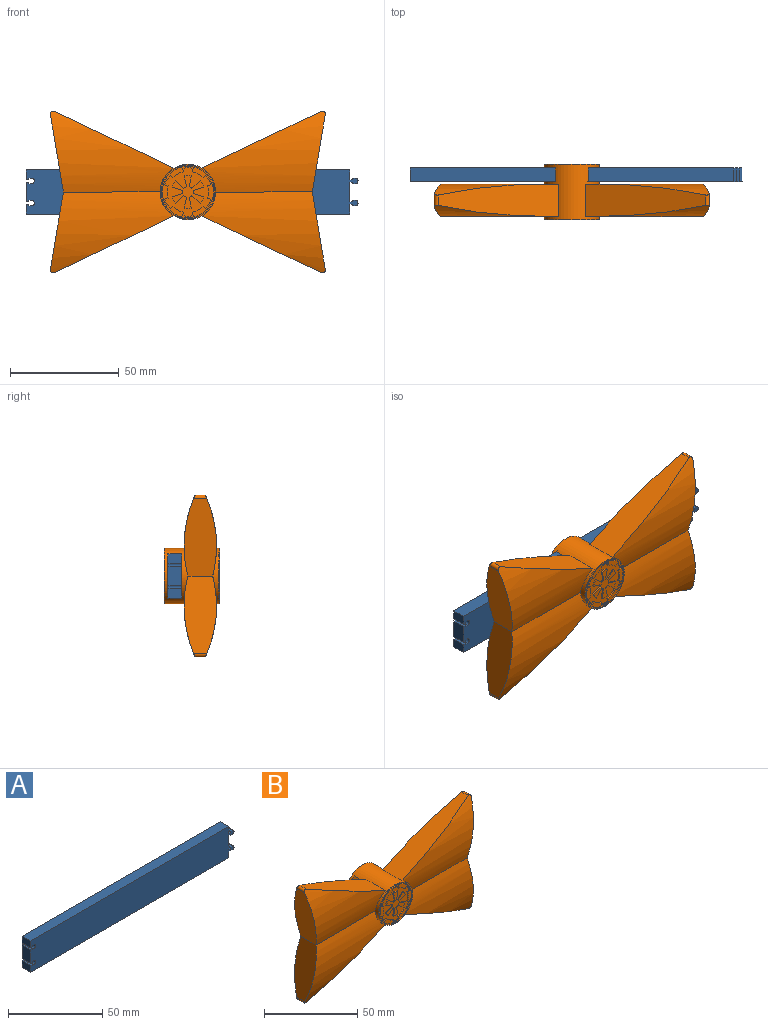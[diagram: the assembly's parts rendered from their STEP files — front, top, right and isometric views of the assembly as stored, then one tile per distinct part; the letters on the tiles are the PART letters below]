
ASSEMBLY  parts=2 mates=1
PART A: 38 faces, bbox 152.4x6.4x20.3 mm
  f0: plane 6.35x1.27mm, normal (0,0,1), area 8.1mm2, adj f1,f35,f36,f37
  f1: plane 6.35x0.64mm, normal (-1,0,0), area 4mm2, adj f0,f2,f36,f37
  f2: plane 6.35x1.27mm, normal (0,0,1), area 8.1mm2, adj f1,f3,f36,f37
  f3: plane 6.35x4.45mm, normal (1,0,0), area 28.2mm2, adj f2,f4,f36,f37
  f4: plane 148.59x6.35mm, normal (0,0,1), area 943.5mm2, adj f3,f5,f36,f37
  f5: plane 6.35x4.45mm, normal (-1,0,0), area 28.2mm2, adj f4,f6,f36,f37
  f6: plane 6.35x1.27mm, normal (0,0,-1), area 8.1mm2, adj f5,f7,f36,f37
  f7: plane 6.35x0.64mm, normal (1,0,0), area 4mm2, adj f6,f8,f36,f37
  f8: plane 6.35x1.27mm, normal (0,0,-1), area 8.1mm2, adj f7,f9,f36,f37
  f9: cylinder r=1.27mm len=6.35mm, axis (0,1,0), area 25.3mm2, adj f8,f10,f36,f37
  f10: plane 6.35x1.27mm, normal (0,0,1), area 8.1mm2, adj f9,f11,f36,f37
  f11: plane 6.35x0.64mm, normal (1,0,0), area 4mm2, adj f10,f12,f36,f37
  f12: plane 6.35x1.27mm, normal (0,0,1), area 8.1mm2, adj f11,f13,f36,f37
  f13: plane 8.89x6.35mm, normal (-1,0,0), area 56.5mm2, adj f12,f14,f36,f37
  f14: plane 6.35x1.27mm, normal (0,0,-1), area 8.1mm2, adj f13,f15,f36,f37
  f15: plane 6.35x0.64mm, normal (1,0,0), area 4mm2, adj f14,f16,f36,f37
  f16: plane 6.35x1.27mm, normal (0,0,-1), area 8.1mm2, adj f15,f17,f36,f37
  f17: cylinder r=1.27mm len=6.35mm, axis (0,1,0), area 25.3mm2, adj f16,f18,f36,f37
  f18: plane 6.35x1.27mm, normal (0,0,1), area 8.1mm2, adj f17,f19,f36,f37
  f19: plane 6.35x0.64mm, normal (1,0,0), area 4mm2, adj f18,f20,f36,f37
  f20: plane 6.35x1.27mm, normal (0,0,1), area 8.1mm2, adj f19,f21,f36,f37
  f21: plane 6.35x4.45mm, normal (-1,0,0), area 28.2mm2, adj f20,f22,f36,f37
  f22: plane 148.59x6.35mm, normal (0,0,-1), area 943.5mm2, adj f21,f23,f36,f37
  f23: plane 6.35x4.45mm, normal (1,0,0), area 28.2mm2, adj f22,f24,f36,f37
  f24: plane 6.35x1.27mm, normal (0,0,-1), area 8.1mm2, adj f23,f25,f36,f37
  f25: plane 6.35x0.64mm, normal (-1,0,0), area 4mm2, adj f24,f26,f36,f37
  f26: plane 6.35x1.27mm, normal (0,0,-1), area 8.1mm2, adj f25,f27,f36,f37
  f27: cylinder r=1.27mm len=6.35mm, axis (0,1,0), area 25.3mm2, adj f26,f28,f36,f37
  f28: plane 6.35x1.27mm, normal (0,0,1), area 8.1mm2, adj f27,f29,f36,f37
  f29: plane 6.35x0.64mm, normal (-1,0,0), area 4mm2, adj f28,f30,f36,f37
  f30: plane 6.35x1.27mm, normal (0,0,1), area 8.1mm2, adj f29,f31,f36,f37
  f31: plane 8.89x6.35mm, normal (1,0,0), area 56.5mm2, adj f30,f32,f36,f37
  f32: plane 6.35x1.27mm, normal (0,0,-1), area 8.1mm2, adj f31,f33,f36,f37
  f33: plane 6.35x0.64mm, normal (-1,0,0), area 4mm2, adj f32,f34,f36,f37
  f34: plane 6.35x1.27mm, normal (0,0,-1), area 8.1mm2, adj f33,f35,f36,f37
  f35: cylinder r=1.27mm len=6.35mm, axis (0,1,0), area 25.3mm2, adj f0,f34,f36,f37
  f36: plane 152.4x20.32mm, normal (0,-1,0), area 3019.3mm2, adj f0,f1,f2,f3,f4,f5,f6,f7
  f37: plane 152.4x20.32mm, normal (0,1,0), area 3019.3mm2, adj f0,f1,f2,f3,f4,f5,f6,f7
PART B: 108 faces, bbox 126.2x25.4x74.4 mm
  f0: cylinder r=12.7mm len=25.4mm, axis (0,1,0), area 1002.8mm2, adj f1,f2,f3,f4,f5,f8,f9,f16
  f1: plane 25.4x25.4mm, normal (0,-1,0), area 34.8mm2, adj f0,f94
  f2: cylinder r=55.88mm len=56.77mm, axis (1,0,0), area 1247.2mm2, adj f0,f3,f6,f7,f8
  f3: cylinder r=55.88mm len=56.77mm, axis (1,0,0), area 1247.2mm2, adj f0,f2,f9,f10,f11
  f4: cylinder r=55.88mm len=56.77mm, axis (1,0,0), area 1247.2mm2, adj f0,f5,f6,f7,f8
  f5: cylinder r=55.88mm len=56.77mm, axis (1,0,0), area 1247.2mm2, adj f0,f4,f9,f10,f11
  f6: plane 35.7x14.91mm, normal (-0.99,0,0.16), area 458.5mm2, adj f2,f4,f7,f11
  f7: cylinder r=1.27mm len=5.99mm, axis (0,1,0), area 14mm2, adj f2,f4,f6,f8
  f8: plane 54.95x26.06mm, normal (0.43,0,-0.9), area 726.8mm2, adj f0,f2,f4,f7
  f9: plane 54.95x26.06mm, normal (0.43,0,0.9), area 726.8mm2, adj f0,f3,f5,f10
  f10: cylinder r=1.27mm len=5.99mm, axis (0,1,0), area 14mm2, adj f3,f5,f9,f11
  f11: plane 35.7x14.91mm, normal (-0.99,0,-0.16), area 458.5mm2, adj f3,f5,f6,f10
  f12: plane 35.7x14.91mm, normal (0.99,0,0.16), area 458.5mm2, adj f13,f15,f17,f19
  f13: cylinder r=1.27mm len=5.99mm, axis (0,1,0), area 14mm2, adj f12,f17,f19,f21
  f14: cylinder r=1.27mm len=5.99mm, axis (0,1,0), area 14mm2, adj f15,f16,f18,f20
  f15: plane 35.7x14.91mm, normal (0.99,0,-0.16), area 458.5mm2, adj f12,f14,f16,f18
  f16: cylinder r=55.88mm len=56.77mm, axis (1,0,0), area 1247.2mm2, adj f0,f14,f15,f17,f20
  f17: cylinder r=55.88mm len=56.77mm, axis (1,0,0), area 1247.2mm2, adj f0,f12,f13,f16,f21
  f18: cylinder r=55.88mm len=56.77mm, axis (1,0,0), area 1247.2mm2, adj f0,f14,f15,f19,f20
  f19: cylinder r=55.88mm len=56.77mm, axis (1,0,0), area 1247.2mm2, adj f0,f12,f13,f18,f21
  f20: plane 54.95x26.06mm, normal (-0.43,0,0.9), area 726.8mm2, adj f0,f14,f16,f18
  f21: plane 54.95x26.06mm, normal (-0.43,0,-0.9), area 726.8mm2, adj f0,f13,f17,f19
  f22: plane 0.64x0.53mm, normal (0.55,0,-0.83), area 0.4mm2, adj f23,f87,f95,f101
  f23: cylinder r=11.11mm len=1.68mm, axis (0,-1,0), area 1.3mm2, adj f22,f24,f95,f101
  f24: plane 1.17x1.07mm, normal (0.68,0,-0.74), area 1mm2, adj f23,f25,f95,f101
  f25: cylinder r=9.53mm len=4.96mm, axis (0,-1,0), area 3.7mm2, adj f24,f26,f95,f101
  f26: plane 1.55x0.64mm, normal (-0.98,0,0.22), area 1mm2, adj f25,f27,f95,f101
  f27: cylinder r=11.11mm len=2.09mm, axis (0,-1,0), area 1.3mm2, adj f26,f28,f95,f101
  f28: plane 0.64x0.64mm, normal (-1,0,0), area 0.4mm2, adj f27,f87,f95,f101
  f29: cylinder r=11.75mm len=9.67mm, axis (0,-1,0), area 7.4mm2, adj f30,f88,f95,f100
  f30: plane 0.64x0.64mm, normal (1,0,0), area 0.4mm2, adj f29,f31,f95,f100
  f31: cylinder r=11.11mm len=2.09mm, axis (0,-1,0), area 1.3mm2, adj f30,f32,f95,f100
  f32: plane 1.55x0.64mm, normal (0.98,0,0.22), area 1mm2, adj f31,f33,f95,f100
  f33: cylinder r=9.53mm len=4.96mm, axis (0,-1,0), area 3.7mm2, adj f32,f34,f95,f100
  f34: plane 1.17x1.07mm, normal (-0.68,0,-0.74), area 1mm2, adj f33,f35,f95,f100
  f35: cylinder r=11.11mm len=1.68mm, axis (0,-1,0), area 1.3mm2, adj f34,f88,f95,f100
  f36: plane 0.64x0.53mm, normal (-0.55,0,0.83), area 0.4mm2, adj f37,f89,f95,f99
  f37: cylinder r=11.75mm len=11.26mm, axis (0,-1,0), area 7.5mm2, adj f36,f38,f95,f99
  f38: plane 0.64x0.53mm, normal (-0.55,0,-0.83), area 0.4mm2, adj f37,f39,f95,f99
  f39: cylinder r=11.11mm len=1.94mm, axis (0,-1,0), area 1.3mm2, adj f38,f40,f95,f99
  f40: plane 1.51x0.64mm, normal (-0.3,0,-0.95), area 1mm2, adj f39,f41,f95,f99
  f41: cylinder r=9.53mm len=5.73mm, axis (0,-1,0), area 3.7mm2, adj f40,f42,f95,f99
  f42: plane 1.51x0.64mm, normal (-0.3,0,0.95), area 1mm2, adj f41,f89,f95,f99
  f43: cylinder r=2.54mm len=1.32mm, axis (0,-1,0), area 1mm2, adj f44,f90,f95,f98
  f44: plane 3.75x3.43mm, normal (0.68,0,-0.74), area 3.2mm2, adj f43,f45,f95,f98
  f45: cylinder r=7.62mm len=2.86mm, axis (0,-1,0), area 2.1mm2, adj f44,f46,f95,f98
  f46: plane 4.85x1.53mm, normal (-0.3,0,0.95), area 3.2mm2, adj f45,f47,f95,f98
  f47: cylinder r=2.54mm len=1.53mm, axis (0,-1,0), area 1mm2, adj f46,f48,f95,f98
  f48: plane 4.85x1.53mm, normal (-0.3,0,-0.95), area 3.2mm2, adj f47,f49,f95,f98
  f49: cylinder r=7.62mm len=2.86mm, axis (0,-1,0), area 2.1mm2, adj f48,f50,f95,f98
  f50: plane 3.75x3.43mm, normal (0.68,0,0.74), area 3.2mm2, adj f49,f51,f95,f98
  f51: cylinder r=2.54mm len=1.32mm, axis (0,-1,0), area 1mm2, adj f50,f52,f95,f98
  f52: plane 4.96x1.1mm, normal (-0.98,0,-0.22), area 3.2mm2, adj f51,f53,f95,f98
  f53: cylinder r=7.62mm len=3.3mm, axis (0,-1,0), area 2.1mm2, adj f52,f54,f95,f98
  f54: plane 4.96x1.1mm, normal (0.98,0,-0.22), area 3.2mm2, adj f53,f55,f95,f98
  f55: cylinder r=2.54mm len=1.32mm, axis (0,-1,0), area 1mm2, adj f54,f56,f95,f98
  f56: plane 3.75x3.43mm, normal (-0.68,0,0.74), area 3.2mm2, adj f55,f57,f95,f98
  f57: cylinder r=7.62mm len=2.86mm, axis (0,-1,0), area 2.1mm2, adj f56,f58,f95,f98
  f58: plane 4.85x1.53mm, normal (0.3,0,-0.95), area 3.2mm2, adj f57,f59,f95,f98
  f59: cylinder r=2.54mm len=1.53mm, axis (0,-1,0), area 1mm2, adj f58,f60,f95,f98
  f60: plane 4.85x1.53mm, normal (0.3,0,0.95), area 3.2mm2, adj f59,f61,f95,f98
  f61: cylinder r=7.62mm len=2.86mm, axis (0,-1,0), area 2.1mm2, adj f60,f62,f95,f98
  f62: plane 3.75x3.43mm, normal (-0.68,0,-0.74), area 3.2mm2, adj f61,f63,f95,f98
  f63: cylinder r=2.54mm len=1.32mm, axis (0,-1,0), area 1mm2, adj f62,f64,f95,f98
  f64: plane 4.96x1.1mm, normal (0.98,0,0.22), area 3.2mm2, adj f63,f65,f95,f98
  f65: cylinder r=7.62mm len=3.3mm, axis (0,-1,0), area 2.1mm2, adj f64,f90,f95,f98
  f66: plane 0.64x0.53mm, normal (0.55,0,-0.83), area 0.4mm2, adj f67,f91,f95,f97
  f67: cylinder r=11.75mm len=11.26mm, axis (0,-1,0), area 7.5mm2, adj f66,f68,f95,f97
  f68: plane 0.64x0.53mm, normal (0.55,0,0.83), area 0.4mm2, adj f67,f69,f95,f97
  f69: cylinder r=11.11mm len=1.94mm, axis (0,-1,0), area 1.3mm2, adj f68,f70,f95,f97
  f70: plane 1.51x0.64mm, normal (0.3,0,0.95), area 1mm2, adj f69,f71,f95,f97
  f71: cylinder r=9.53mm len=5.73mm, axis (0,-1,0), area 3.7mm2, adj f70,f72,f95,f97
  f72: plane 1.51x0.64mm, normal (0.3,0,-0.95), area 1mm2, adj f71,f91,f95,f97
  f73: cylinder r=9.53mm len=4.96mm, axis (0,-1,0), area 3.7mm2, adj f74,f92,f95,f96
  f74: plane 1.55x0.64mm, normal (0.98,0,-0.22), area 1mm2, adj f73,f75,f95,f96
  f75: cylinder r=11.11mm len=2.09mm, axis (0,-1,0), area 1.3mm2, adj f74,f76,f95,f96
  f76: plane 0.64x0.64mm, normal (1,0,0), area 0.4mm2, adj f75,f77,f95,f96
  f77: cylinder r=11.75mm len=9.67mm, axis (0,-1,0), area 7.4mm2, adj f76,f78,f95,f96
  f78: plane 0.64x0.53mm, normal (-0.55,0,0.83), area 0.4mm2, adj f77,f79,f95,f96
  f79: cylinder r=11.11mm len=1.68mm, axis (0,-1,0), area 1.3mm2, adj f78,f92,f95,f96
  f80: plane 1.17x1.07mm, normal (0.68,0,0.74), area 1mm2, adj f81,f93,f95,f102
  f81: cylinder r=11.11mm len=1.68mm, axis (0,-1,0), area 1.3mm2, adj f80,f82,f95,f102
  f82: plane 0.64x0.53mm, normal (0.55,0,0.83), area 0.4mm2, adj f81,f83,f95,f102
  f83: cylinder r=11.75mm len=9.67mm, axis (0,-1,0), area 7.4mm2, adj f82,f84,f95,f102
  f84: plane 0.64x0.64mm, normal (-1,0,0), area 0.4mm2, adj f83,f85,f95,f102
  f85: cylinder r=11.11mm len=2.09mm, axis (0,-1,0), area 1.3mm2, adj f84,f86,f95,f102
  f86: plane 1.55x0.64mm, normal (-0.98,0,-0.22), area 1mm2, adj f85,f93,f95,f102
  f87: cylinder r=11.75mm len=9.67mm, axis (0,-1,0), area 7.4mm2, adj f22,f28,f95,f101
  f88: plane 0.64x0.53mm, normal (-0.55,0,-0.83), area 0.4mm2, adj f29,f35,f95,f100
  f89: cylinder r=11.11mm len=1.94mm, axis (0,-1,0), area 1.3mm2, adj f36,f42,f95,f99
  f90: plane 4.96x1.1mm, normal (-0.98,0,0.22), area 3.2mm2, adj f43,f65,f95,f98
  f91: cylinder r=11.11mm len=1.94mm, axis (0,-1,0), area 1.3mm2, adj f66,f72,f95,f97
  f92: plane 1.17x1.07mm, normal (-0.68,0,0.74), area 1mm2, adj f73,f79,f95,f96
  f93: cylinder r=9.53mm len=4.96mm, axis (0,-1,0), area 3.7mm2, adj f80,f86,f95,f102
  f94: cylinder r=12.26mm len=24.51mm, axis (0,-1,0), area 48.9mm2, adj f1,f95
  f95: plane 24.51x24.51mm, normal (0,-1,0), area 280.8mm2, adj f22,f23,f24,f25,f26,f27,f28,f29
  f96: plane 9.67x5.91mm, normal (0,-1,0), area 17.2mm2, adj f73,f74,f75,f76,f77,f78,f79,f92
  f97: plane 11.26x2.66mm, normal (0,-1,0), area 17.2mm2, adj f66,f67,f68,f69,f70,f71,f72,f91
  f98: plane 15.24x14.53mm, normal (0,-1,0), area 87.8mm2, adj f43,f44,f45,f46,f47,f48,f49,f50
  f99: plane 11.26x2.66mm, normal (0,-1,0), area 17.2mm2, adj f36,f37,f38,f39,f40,f41,f42,f89
  f100: plane 9.67x5.91mm, normal (0,-1,0), area 17.2mm2, adj f29,f30,f31,f32,f33,f34,f35,f88
  f101: plane 9.67x5.91mm, normal (0,-1,0), area 17.2mm2, adj f22,f23,f24,f25,f26,f27,f28,f87
  f102: plane 9.67x5.91mm, normal (0,-1,0), area 17.2mm2, adj f80,f81,f82,f83,f84,f85,f86,f93
  f103: plane 25.4x25.4mm, normal (0,1,0), area 506.7mm2, adj f0
  f104: plane 25.4x20.32mm, normal (0,-1,0), area 454mm2, adj f0,f105,f107
  f105: plane 15.24x6.35mm, normal (0,0,-1), area 96.8mm2, adj f0,f104,f106
  f106: plane 25.4x20.32mm, normal (0,1,0), area 454mm2, adj f0,f105,f107
  f107: plane 15.24x6.35mm, normal (0,0,1), area 96.8mm2, adj f0,f104,f106
PLACE A t=(-2.92,-33.39,47.04)mm
PLACE B rot(axis=(0,0,1),0deg) t=(-4.82,-48.25,47.04)mm
MATE slider B.f107 <-> A.f22  axis (0,0,1) through (-4.82,-36.57,36.88)mm
